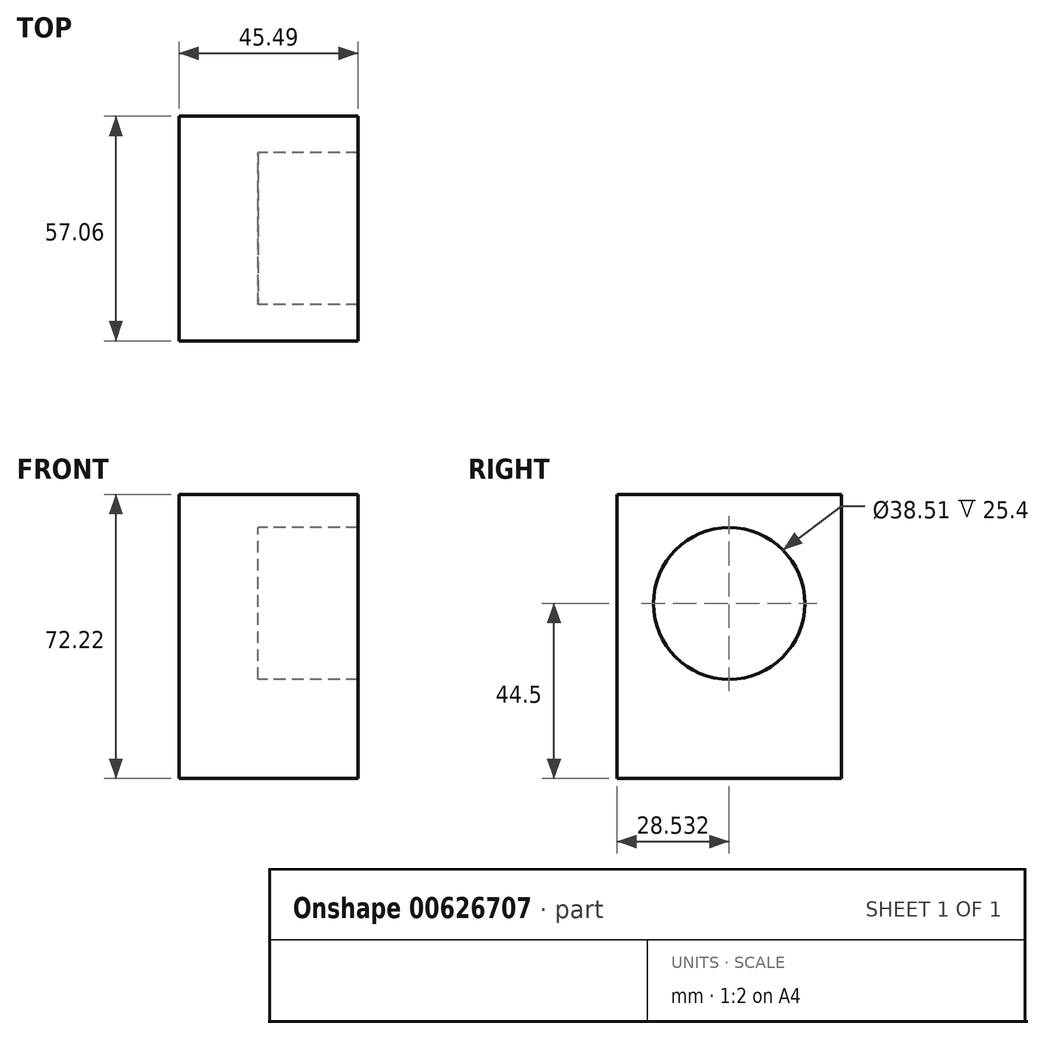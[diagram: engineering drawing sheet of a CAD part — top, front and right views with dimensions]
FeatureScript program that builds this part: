
annotation { "Feature Type Name" : "Feature", "Feature Type Description" : "" }
export const myFeature = defineFeature(function(context is Context, id is Id, definition is map)
    precondition{}
    {
        {
            var Q0;
            Q0=qCreatedBy(makeId("Front.planeOp"),FACE);
            var sketch = newSketch(context, id + "F0", { "sketchPlane" : qUnion([Q0])});
            skLineSegment(sketch, "E0.bottom", {"start": v(-42.82, 52.24) * mm, "end": v(-22.73, 52.24) * mm});
            skLineSegment(sketch, "E0.top", {"start": v(-42.82, -19.98) * mm, "end": v(-22.73, -19.98) * mm});
            skLineSegment(sketch, "E0.left", {"start": v(-42.82, 52.24) * mm, "end": v(-42.82, -19.98) * mm});
            skLineSegment(sketch, "E0.right", {"start": v(-22.73, 52.24) * mm, "end": v(-22.73, -19.98) * mm});
            skSolve(sketch);
        }
        {
            var Q0;
            Q0=makeQuery(id+"F0.imprint","IMPRINT",FACE,{"disambiguationData":[TD([[makeQuery(id+"F0.imprint","IMPRINT",EDGE,{"derivedFrom":sQuery(id+"F0.wireOp",EDGE,"E0.bottom")}),-1.0]])]});
            extrude(context, id + "F1", {"entities" : qUnion([Q0]), "depth" : 57.06 * mm, "offsetDistance" : 25.4 * mm});
        }
        {
            var Q0;
            Q0=makeQuery(id+"F1.opExtrude","SWEPT_FACE",FACE,{"disambiguationData":[OSD([sQuery(id+"F0.wireOp",EDGE,"E0.right")])]});
            var sketch = newSketch(context, id + "F2", { "sketchPlane" : qUnion([Q0])});
            skCircle(sketch, "E1", {"center": v(-28.53, 24.52) * mm, "radius": 19.26 * mm});
            skPoint(sketch, "E1.centerSnap0", {"position": v(-28.53, 52.24) * mm});
            skSolve(sketch);
        }
        {
            var Q0;
            Q0=makeQuery(id+"F2.imprint","IMPRINT",FACE,{"disambiguationData":[TD([[makeQuery(id+"F2.imprint","IMPRINT",EDGE,{"derivedFrom":sQuery(id+"F2.wireOp",EDGE,"E1")}),-1.0]])]});
            extrude(context, id + "F3", {"entities" : qUnion([Q0]), "operationType" : NewBodyOperationType.ADD, "depth" : 25.4 * mm, "offsetDistance" : 25.4 * mm});
        }
    });
